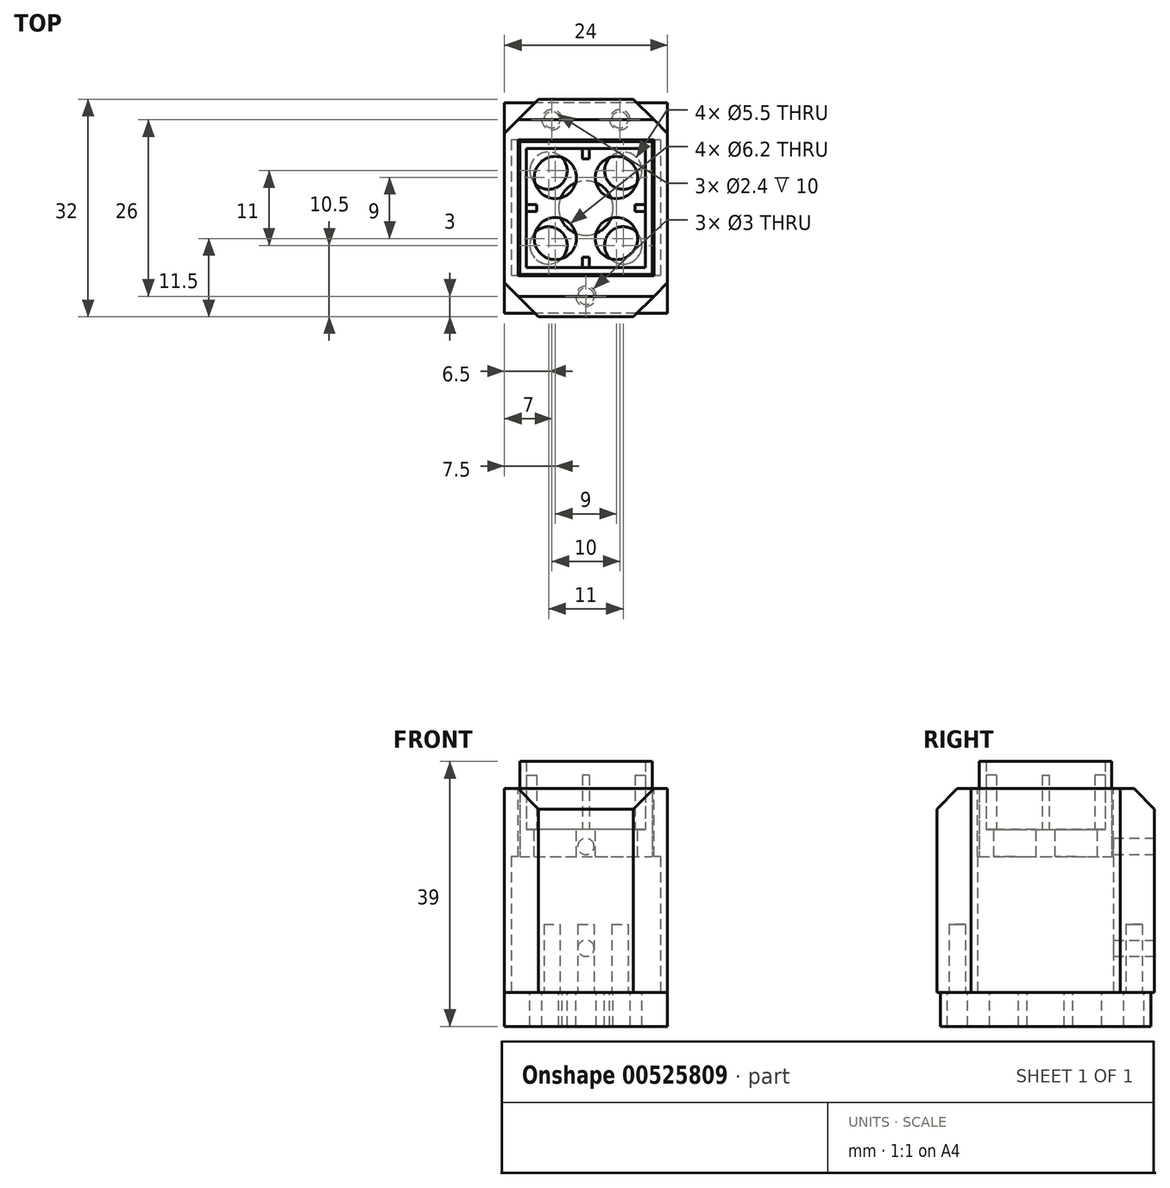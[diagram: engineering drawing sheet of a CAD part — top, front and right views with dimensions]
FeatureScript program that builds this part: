
annotation { "Feature Type Name" : "Feature", "Feature Type Description" : "" }
export const myFeature = defineFeature(function(context is Context, id is Id, definition is map)
    precondition{}
    {
        {
            var Q0;
            Q0=qCreatedBy(makeId("Top.planeOp"),FACE);
            var sketch = newSketch(context, id + "F0", { "sketchPlane" : qUnion([Q0])});
            skPoint(sketch, "E0.middle", {"position": v(0, 0) * mm});
            skLineSegment(sketch, "E1.bottom", {"start": v(9.75, -9.75) * mm, "end": v(-9.75, -9.75) * mm});
            skLineSegment(sketch, "E1.top", {"start": v(9.75, 9.75) * mm, "end": v(-9.75, 9.75) * mm});
            skLineSegment(sketch, "E1.left", {"start": v(9.75, -9.75) * mm, "end": v(9.75, 9.75) * mm});
            skLineSegment(sketch, "E1.right", {"start": v(-9.75, -9.75) * mm, "end": v(-9.75, 9.75) * mm});
            skSolve(sketch);
        }
        {
            var Q0;
            Q0=qSketchRegion(id+"F0",true);
            extrude(context, id + "F1", {"entities" : qUnion([Q0]), "depth" : 13 * mm, "offsetDistance" : 25 * mm});
        }
        {
            var Q0;
            Q0=makeQuery(id+"F1.opExtrude","CAP_FACE",FACE,{"disambiguationData":[OSD([sQuery(id+"F0.wireOp",EDGE,"E1.bottom"),sQuery(id+"F0.wireOp",EDGE,"E1.top"),sQuery(id+"F0.wireOp",EDGE,"E1.left"),sQuery(id+"F0.wireOp",EDGE,"E1.right")])],"isStart":false});
            var sketch = newSketch(context, id + "F2", { "sketchPlane" : qUnion([Q0])});
            skLineSegment(sketch, "E2.bottom", {"start": v(9.75, -9.75) * mm, "end": v(-9.75, -9.75) * mm});
            skLineSegment(sketch, "E2.top", {"start": v(9.75, 9.75) * mm, "end": v(-9.75, 9.75) * mm});
            skLineSegment(sketch, "E2.left", {"start": v(9.75, -9.75) * mm, "end": v(9.75, 9.75) * mm});
            skLineSegment(sketch, "E2.right", {"start": v(-9.75, -9.75) * mm, "end": v(-9.75, 9.75) * mm});
            skPoint(sketch, "E2.middle", {"position": v(0, 0) * mm});
            skLineSegment(sketch, "E3.bottom", {"start": v(8.75, -8.75) * mm, "end": v(-8.75, -8.75) * mm});
            skLineSegment(sketch, "E3.top", {"start": v(8.75, 8.75) * mm, "end": v(-8.75, 8.75) * mm});
            skLineSegment(sketch, "E3.left", {"start": v(8.75, -8.75) * mm, "end": v(8.75, 8.75) * mm});
            skLineSegment(sketch, "E3.right", {"start": v(-8.75, -8.75) * mm, "end": v(-8.75, 8.75) * mm});
            skSolve(sketch);
        }
        {
            var Q0;
            Q0=qSketchRegion(id+"F2",true);
            extrude(context, id + "F3", {"entities" : qUnion([Q0]), "operationType" : NewBodyOperationType.ADD, "depth" : 10 * mm, "offsetDistance" : 25 * mm});
        }
        {
            var Q0;
            Q0=makeQuery(id+"F1.opExtrude","CAP_FACE",FACE,{"disambiguationData":[OSD([sQuery(id+"F0.wireOp",EDGE,"E1.bottom"),sQuery(id+"F0.wireOp",EDGE,"E1.top"),sQuery(id+"F0.wireOp",EDGE,"E1.left"),sQuery(id+"F0.wireOp",EDGE,"E1.right")])],"isStart":false});
            var sketch = newSketch(context, id + "F4", { "sketchPlane" : qUnion([Q0])});
            skLineSegment(sketch, "E4.bottom", {"start": v(-0.5, 8.75) * mm, "end": v(0.5, 8.75) * mm});
            skLineSegment(sketch, "E4.top", {"start": v(-0.5, -8.75) * mm, "end": v(0.5, -8.75) * mm});
            skLineSegment(sketch, "E4.left", {"start": v(-0.5, 8.75) * mm, "end": v(-0.5, 7.25) * mm});
            skLineSegment(sketch, "E4.right", {"start": v(0.5, 8.75) * mm, "end": v(0.5, 7.25) * mm});
            skLineSegment(sketch, "E5.bottom", {"start": v(-8.75, 0.5) * mm, "end": v(-7.25, 0.5) * mm});
            skLineSegment(sketch, "E5.top", {"start": v(-8.75, -0.5) * mm, "end": v(-7.25, -0.5) * mm});
            skLineSegment(sketch, "E5.left", {"start": v(-8.75, 0.5) * mm, "end": v(-8.75, -0.5) * mm});
            skLineSegment(sketch, "E5.right", {"start": v(8.75, 0.5) * mm, "end": v(8.75, -0.5) * mm});
            skLineSegment(sketch, "E6.trimOffspring", {"start": v(-0.5, -7.25) * mm, "end": v(-0.5, -8.75) * mm});
            skLineSegment(sketch, "E7.trimOffspring", {"start": v(0.5, -7.25) * mm, "end": v(0.5, -8.75) * mm});
            skLineSegment(sketch, "E8.trimOffspring", {"start": v(7.25, 0.5) * mm, "end": v(8.75, 0.5) * mm});
            skLineSegment(sketch, "E9.trimOffspring", {"start": v(7.25, -0.5) * mm, "end": v(8.75, -0.5) * mm});
            skLineSegment(sketch, "E10.bottom", {"start": v(0.5, -7.25) * mm, "end": v(-0.5, -7.25) * mm});
            skLineSegment(sketch, "E10.top", {"start": v(0.5, 7.25) * mm, "end": v(-0.5, 7.25) * mm});
            skLineSegment(sketch, "E10.left", {"start": v(7.25, -0.5) * mm, "end": v(7.25, 0.5) * mm});
            skLineSegment(sketch, "E10.right", {"start": v(-7.25, -0.5) * mm, "end": v(-7.25, 0.5) * mm});
            skPoint(sketch, "E10.middle", {"position": v(0, 0) * mm});
            skPoint(sketch, "E11.orphan", {"position": v(7.25, 7.25) * mm});
            skPoint(sketch, "E12.orphan", {"position": v(7.25, -7.25) * mm});
            skPoint(sketch, "E13.orphan", {"position": v(-7.25, 7.25) * mm});
            skPoint(sketch, "E14.orphan", {"position": v(-7.25, -7.25) * mm});
            skSolve(sketch);
        }
        {
            var Q0;
            Q0=qSketchRegion(id+"F4",true);
            extrude(context, id + "F5", {"entities" : qUnion([Q0]), "operationType" : NewBodyOperationType.ADD, "depth" : 8 * mm, "offsetDistance" : 25 * mm});
        }
        {
            var Q0;
            Q0=makeQuery(id+"F1.opExtrude","CAP_FACE",FACE,{"disambiguationData":[OSD([sQuery(id+"F0.wireOp",EDGE,"E1.bottom"),sQuery(id+"F0.wireOp",EDGE,"E1.top"),sQuery(id+"F0.wireOp",EDGE,"E1.left"),sQuery(id+"F0.wireOp",EDGE,"E1.right")])],"isStart":false});
            var sketch = newSketch(context, id + "F6", { "sketchPlane" : qUnion([Q0])});
            skCircle(sketch, "E15", {"center": v(-4.5, 4.5) * mm, "radius": 3.1 * mm});
            skCircle(sketch, "E16", {"center": v(-4.5, -4.5) * mm, "radius": 3.1 * mm});
            skCircle(sketch, "E17", {"center": v(4.5, 4.5) * mm, "radius": 3.1 * mm});
            skCircle(sketch, "E18", {"center": v(4.5, -4.5) * mm, "radius": 3.1 * mm});
            skSolve(sketch);
        }
        {
            var Q0;
            Q0=qSketchRegion(id+"F6",true);
            extrude(context, id + "F7", {"entities" : qUnion([Q0]), "operationType" : NewBodyOperationType.REMOVE, "oppositeDirection" : true, "depth" : 19 * mm, "offsetDistance" : 25 * mm});
        }
        {
            var Q0;
            Q0=makeQuery(id+"F1.opExtrude","CAP_FACE",FACE,{"disambiguationData":[OSD([sQuery(id+"F0.wireOp",EDGE,"E1.bottom"),sQuery(id+"F0.wireOp",EDGE,"E1.top"),sQuery(id+"F0.wireOp",EDGE,"E1.left"),sQuery(id+"F0.wireOp",EDGE,"E1.right")])],"isStart":true});
            var sketch = newSketch(context, id + "F8", { "sketchPlane" : qUnion([Q0])});
            skLineSegment(sketch, "E19.bottom", {"start": v(-9.75, -9.75) * mm, "end": v(-10.75, -9.75) * mm});
            skLineSegment(sketch, "E19.top", {"start": v(-9.75, 9.75) * mm, "end": v(-10.75, 9.75) * mm});
            skLineSegment(sketch, "E19.left", {"start": v(-9.75, -9.75) * mm, "end": v(-9.75, 9.75) * mm});
            skLineSegment(sketch, "E19.right", {"start": v(-10.75, -9.75) * mm, "end": v(-10.75, 9.75) * mm});
            skLineSegment(sketch, "E20.bottom", {"start": v(9.75, -9.75) * mm, "end": v(10.75, -9.75) * mm});
            skLineSegment(sketch, "E20.top", {"start": v(9.75, 9.75) * mm, "end": v(10.75, 9.75) * mm});
            skLineSegment(sketch, "E20.left", {"start": v(9.75, -9.75) * mm, "end": v(9.75, 9.75) * mm});
            skLineSegment(sketch, "E20.right", {"start": v(10.75, -9.75) * mm, "end": v(10.75, 9.75) * mm});
            skSolve(sketch);
        }
        {
            var Q0;
            Q0=qSketchRegion(id+"F8",true);
            extrude(context, id + "F9", {"entities" : qUnion([Q0]), "operationType" : NewBodyOperationType.ADD, "oppositeDirection" : true, "depth" : 9 * mm, "offsetDistance" : 25 * mm});
        }
        {
            var Q0;
            Q0=makeQuery(id+"F9.boolean.opBoolean","MERGE",FACE,{"derivedFrom":[makeQuery(id+"F1.opExtrude","CAP_FACE",FACE,{"disambiguationData":[OSD([sQuery(id+"F0.wireOp",EDGE,"E1.bottom"),sQuery(id+"F0.wireOp",EDGE,"E1.top"),sQuery(id+"F0.wireOp",EDGE,"E1.left"),sQuery(id+"F0.wireOp",EDGE,"E1.right")])],"isStart":true}),makeQuery(id+"F9.opExtrude","CAP_FACE",FACE,{"disambiguationData":[OSD([sQuery(id+"F8.wireOp",EDGE,"E19.bottom"),sQuery(id+"F8.wireOp",EDGE,"E19.top"),sQuery(id+"F8.wireOp",EDGE,"E19.left"),sQuery(id+"F8.wireOp",EDGE,"E19.right")])],"isStart":true}),makeQuery(id+"F9.opExtrude","CAP_FACE",FACE,{"disambiguationData":[OSD([sQuery(id+"F8.wireOp",EDGE,"E20.bottom"),sQuery(id+"F8.wireOp",EDGE,"E20.top"),sQuery(id+"F8.wireOp",EDGE,"E20.left"),sQuery(id+"F8.wireOp",EDGE,"E20.right")])],"isStart":true})]});
            var sketch = newSketch(context, id + "F10", { "sketchPlane" : qUnion([Q0])});
            skCircle(sketch, "E21", {"center": v(0, 0) * mm, "radius": 2.55 * mm});
            skSolve(sketch);
        }
        {
            var Q0;
            Q0=qSketchRegion(id+"F10",true);
            extrude(context, id + "F11", {"entities" : qUnion([Q0]), "operationType" : NewBodyOperationType.REMOVE, "oppositeDirection" : true, "depth" : 3 * mm, "offsetDistance" : 25 * mm});
        }
        {
            var Q0;
            Q0=qCreatedBy(makeId("Top.planeOp"),FACE);
            cPlane(context, id + "F12", {"entities" : qUnion([Q0]), "cplaneType" : CPlaneType.OFFSET, "offset" : 19 * mm, "width" : 150 * mm, "height" : 150 * mm});
        }
        {
            var Q0;
            Q0=qCreatedBy(id+"F12.planeOp",FACE);
            var sketch = newSketch(context, id + "F13", { "sketchPlane" : qUnion([Q0])});
            skLineSegment(sketch, "E22.bottom", {"start": v(12, -11) * mm, "end": v(-12, -11) * mm});
            skLineSegment(sketch, "E22.top", {"start": v(12, 11) * mm, "end": v(-12, 11) * mm});
            skLineSegment(sketch, "E22.left", {"start": v(12, -11) * mm, "end": v(12, 11) * mm});
            skLineSegment(sketch, "E22.right", {"start": v(-12, -11) * mm, "end": v(-12, 11) * mm});
            skPoint(sketch, "E22.middle", {"position": v(0, 0) * mm});
            skLineSegment(sketch, "E23.bottom", {"start": v(10, -10) * mm, "end": v(-10, -10) * mm});
            skLineSegment(sketch, "E23.top", {"start": v(10, 10) * mm, "end": v(-10, 10) * mm});
            skLineSegment(sketch, "E23.left", {"start": v(10, -10) * mm, "end": v(10, 10) * mm});
            skLineSegment(sketch, "E23.right", {"start": v(-10, -10) * mm, "end": v(-10, 10) * mm});
            skLineSegment(sketch, "E24.bottom", {"start": v(-5, -11) * mm, "end": v(5, -11) * mm});
            skLineSegment(sketch, "E24.top", {"start": v(-5, -16) * mm, "end": v(5, -16) * mm});
            skLineSegment(sketch, "E24.left", {"start": v(-5, -11) * mm, "end": v(-5, -16) * mm});
            skLineSegment(sketch, "E24.right", {"start": v(5, -11) * mm, "end": v(5, -16) * mm});
            skLineSegment(sketch, "E25.bottom", {"start": v(-5, 11) * mm, "end": v(5, 11) * mm});
            skLineSegment(sketch, "E25.top", {"start": v(-5, 16) * mm, "end": v(5, 16) * mm});
            skLineSegment(sketch, "E25.left", {"start": v(-5, 11) * mm, "end": v(-5, 16) * mm});
            skLineSegment(sketch, "E25.right", {"start": v(5, 11) * mm, "end": v(5, 16) * mm});
            skSolve(sketch);
        }
        {
            var Q0;
            Q0 = qSketchRegion(id + "F13", true);
            extrude(context, id + "F14", {"entities" : qUnion([Q0]), "oppositeDirection" : true, "depth" : 30 * mm, "offsetDistance" : 25 * mm});
        }
        {
            var Q0;
            Q0=makeQuery(id+"F14.opExtrude","CAP_FACE",FACE,{"disambiguationData":[OSD([sQuery(id+"F13.wireOp",EDGE,"E22.bottom"),sQuery(id+"F13.wireOp",EDGE,"E22.top"),sQuery(id+"F13.wireOp",EDGE,"E22.left"),sQuery(id+"F13.wireOp",EDGE,"E22.right"),sQuery(id+"F13.wireOp",EDGE,"E23.bottom"),sQuery(id+"F13.wireOp",EDGE,"E23.top"),sQuery(id+"F13.wireOp",EDGE,"E23.left"),sQuery(id+"F13.wireOp",EDGE,"E23.right")])],"isStart":false});
            var sketch = newSketch(context, id + "F15", { "sketchPlane" : qUnion([Q0])});
            skLineSegment(sketch, "E26.bottom", {"start": v(11, -10) * mm, "end": v(-11, -10) * mm});
            skLineSegment(sketch, "E26.top", {"start": v(11, 10) * mm, "end": v(-11, 10) * mm});
            skLineSegment(sketch, "E26.left", {"start": v(11, -10) * mm, "end": v(11, 10) * mm});
            skLineSegment(sketch, "E26.right", {"start": v(-11, -10) * mm, "end": v(-11, 10) * mm});
            skPoint(sketch, "E26.middle", {"position": v(0, 0) * mm});
            skSolve(sketch);
        }
        {
            var Q0;
            Q0 = qSketchRegion(id + "F15", true);
            extrude(context, id + "F16", {"entities" : qUnion([Q0]), "operationType" : NewBodyOperationType.REMOVE, "oppositeDirection" : true, "depth" : 20 * mm, "offsetDistance" : 25 * mm});
        }
        {
            var Q0;
            Q0=makeQuery(id+"F14.opExtrude","SWEPT_FACE",FACE,{"disambiguationData":[OSD([sQuery(id+"F13.wireOp",EDGE,"E25.top")])]});
            var sketch = newSketch(context, id + "F17", { "sketchPlane" : qUnion([Q0])});
            skCircle(sketch, "E27", {"center": v(0, 10.5) * mm, "radius": 1.2 * mm});
            skCircle(sketch, "E28", {"center": v(0, -4.5) * mm, "radius": 1.2 * mm});
            skSolve(sketch);
        }
        {
            var Q0;
            Q0 = qSketchRegion(id + "F17", true);
            extrude(context, id + "F18", {"entities" : qUnion([Q0]), "operationType" : NewBodyOperationType.REMOVE, "oppositeDirection" : true, "depth" : 6 * mm, "offsetDistance" : 25 * mm});
        }
        {
            var Q0;
            Q0=makeQuery(id+"F14.opExtrude","SWEPT_EDGE",EDGE,{"disambiguationData":[OSD([sQuery(id+"F13.wireOp",EDGE,"E22.top"),sQuery(id+"F13.wireOp",EDGE,"E25.bottom"),sQuery(id+"F13.wireOp",EDGE,"E25.right")])]});
            var Q1;
            Q1=makeQuery(id+"F14.opExtrude","SWEPT_EDGE",EDGE,{"disambiguationData":[OSD([sQuery(id+"F13.wireOp",EDGE,"E22.top"),sQuery(id+"F13.wireOp",EDGE,"E25.bottom"),sQuery(id+"F13.wireOp",EDGE,"E25.left")])]});
            var Q2;
            Q2=makeQuery(id+"F14.opExtrude","SWEPT_EDGE",EDGE,{"disambiguationData":[OSD([sQuery(id+"F13.wireOp",EDGE,"E22.bottom"),sQuery(id+"F13.wireOp",EDGE,"E24.bottom"),sQuery(id+"F13.wireOp",EDGE,"E24.left")])]});
            var Q3;
            Q3=makeQuery(id+"F14.opExtrude","SWEPT_EDGE",EDGE,{"disambiguationData":[OSD([sQuery(id+"F13.wireOp",EDGE,"E22.bottom"),sQuery(id+"F13.wireOp",EDGE,"E24.bottom"),sQuery(id+"F13.wireOp",EDGE,"E24.right")])]});
            chamfer(context, id + "F19", {"entities" : qUnion([Q0, Q1, Q2, Q3]), "width" : 7 * mm, "tangentPropagation" : true});
        }
        {
            var Q0;
            Q0=makeQuery(id+"F14.opExtrude","CAP_FACE",FACE,{"disambiguationData":[OSD([sQuery(id+"F13.wireOp",EDGE,"E22.bottom"),sQuery(id+"F13.wireOp",EDGE,"E22.top"),sQuery(id+"F13.wireOp",EDGE,"E22.left"),sQuery(id+"F13.wireOp",EDGE,"E22.right"),sQuery(id+"F13.wireOp",EDGE,"E23.bottom"),sQuery(id+"F13.wireOp",EDGE,"E23.top"),sQuery(id+"F13.wireOp",EDGE,"E23.left"),sQuery(id+"F13.wireOp",EDGE,"E23.right"),sQuery(id+"F13.wireOp",EDGE,"E24.top"),sQuery(id+"F13.wireOp",EDGE,"E24.left"),sQuery(id+"F13.wireOp",EDGE,"E24.right"),sQuery(id+"F13.wireOp",EDGE,"E25.top"),sQuery(id+"F13.wireOp",EDGE,"E25.left"),sQuery(id+"F13.wireOp",EDGE,"E25.right")])],"isStart":false});
            var sketch = newSketch(context, id + "F20", { "sketchPlane" : qUnion([Q0])});
            skCircle(sketch, "E29", {"center": v(0, 13) * mm, "radius": 1.2 * mm});
            skCircle(sketch, "E30", {"center": v(-5, -13) * mm, "radius": 1.2 * mm});
            skCircle(sketch, "E31", {"center": v(5, -13) * mm, "radius": 1.2 * mm});
            skSolve(sketch);
        }
        {
            var Q0;
            Q0 = qSketchRegion(id + "F20", true);
            extrude(context, id + "F21", {"entities" : qUnion([Q0]), "operationType" : NewBodyOperationType.REMOVE, "oppositeDirection" : true, "depth" : 10 * mm, "offsetDistance" : 25 * mm});
        }
        {
            var Q0;
            Q0=makeQuery(id+"F14.opExtrude","CAP_FACE",FACE,{"disambiguationData":[OSD([sQuery(id+"F13.wireOp",EDGE,"E22.bottom"),sQuery(id+"F13.wireOp",EDGE,"E22.top"),sQuery(id+"F13.wireOp",EDGE,"E22.left"),sQuery(id+"F13.wireOp",EDGE,"E22.right"),sQuery(id+"F13.wireOp",EDGE,"E23.bottom"),sQuery(id+"F13.wireOp",EDGE,"E23.top"),sQuery(id+"F13.wireOp",EDGE,"E23.left"),sQuery(id+"F13.wireOp",EDGE,"E23.right"),sQuery(id+"F13.wireOp",EDGE,"E24.top"),sQuery(id+"F13.wireOp",EDGE,"E24.left"),sQuery(id+"F13.wireOp",EDGE,"E24.right"),sQuery(id+"F13.wireOp",EDGE,"E25.top"),sQuery(id+"F13.wireOp",EDGE,"E25.left"),sQuery(id+"F13.wireOp",EDGE,"E25.right")])],"isStart":false});
            cPlane(context, id + "F22", {"entities" : qUnion([Q0]), "cplaneType" : CPlaneType.OFFSET, "offset" : 0 * mm, "width" : 150 * mm, "height" : 150 * mm});
        }
        {
            var Q0;
            Q0=qCreatedBy(id+"F22.planeOp",FACE);
            var sketch = newSketch(context, id + "F23", { "sketchPlane" : qUnion([Q0])});
            skLineSegment(sketch, "E32.bottom", {"start": v(12, -15.5) * mm, "end": v(-12, -15.5) * mm});
            skLineSegment(sketch, "E32.top", {"start": v(12, 15.5) * mm, "end": v(-12, 15.5) * mm});
            skLineSegment(sketch, "E32.left", {"start": v(12, -15.5) * mm, "end": v(12, 15.5) * mm});
            skLineSegment(sketch, "E32.right", {"start": v(-12, -15.5) * mm, "end": v(-12, 15.5) * mm});
            skPoint(sketch, "E32.middle", {"position": v(0, 0) * mm});
            skCircle(sketch, "E33", {"center": v(0, 0) * mm, "radius": 4 * mm});
            skCircle(sketch, "E34", {"center": v(-5.5, 5.5) * mm, "radius": 2.75 * mm});
            skCircle(sketch, "E35", {"center": v(5.5, 5.5) * mm, "radius": 2.75 * mm});
            skCircle(sketch, "E36", {"center": v(-5.5, -5.5) * mm, "radius": 2.75 * mm});
            skCircle(sketch, "E37", {"center": v(5.5, -5.5) * mm, "radius": 2.75 * mm});
            skCircle(sketch, "E38", {"center": v(0, 13) * mm, "radius": 1.5 * mm});
            skCircle(sketch, "E39", {"center": v(-5, -13) * mm, "radius": 1.5 * mm});
            skCircle(sketch, "E40", {"center": v(5, -13) * mm, "radius": 1.5 * mm});
            skSolve(sketch);
        }
        {
            var Q0;
            Q0 = qSketchRegion(id + "F23", true);
            extrude(context, id + "F24", {"entities" : qUnion([Q0]), "depth" : 5 * mm, "offsetDistance" : 25 * mm});
        }
        {
            var Q0;
            Q0=makeQuery(id+"F14.opExtrude","CAP_EDGE",EDGE,{"disambiguationData":[OSD([sQuery(id+"F13.wireOp",EDGE,"E25.top")])],"isStart":true});
            var Q1;
            Q1=makeQuery(id+"F14.opExtrude","CAP_EDGE",EDGE,{"disambiguationData":[OSD([sQuery(id+"F13.wireOp",EDGE,"E24.top")])],"isStart":true});
            chamfer(context, id + "F25", {"entities" : qUnion([Q0, Q1]), "width" : 3 * mm, "tangentPropagation" : true});
        }
    });
